# Revit family: PRD_FrankeWS_Mrrs_Mirror_CHRH401-CHRH601
name_source: partatom
category: Furniture
revit_build: Autodesk Revit 2018 (Build: 20190510_1515(x64)
units: mm (PartAtom-declared; Revit-internal decimal feet)

## family parameters
Cut with Voids When Loaded = No
Host = Face
OmniClass Number = 23.40.20.21
OmniClass Title = Toilet and Bath Specialties
Room Calculation Point = No
Shared = No

## types (3) — shared parameters
AssetType = Fixed
Category = Pr_25_71_53_06, Bathroom mirrors
Color = Stainless steel
Default Elevation = 1100 mm
DurationUnit = year
Finish = High polished
Form = Wall mounted
IfcExportAs = IfcFurnitureType
IfcExportType = NOTDEFINED
IntegralAccessories = Stainless steel screws and dowels incl.
MainColor = Stainless steel
Manufacturer = KWC Group AG
ManufacturerName = KWC Group AG
ManufacturerURL = www.kwc.com
Material = Stainless steel
MaterialsGlazing = Stainless steel 1.4301
MirrorMaterial = PRD_AR_StainlessSteel_HighPolished
NBSDescription = Mirrors
NBSReference = 45-35-72/336
NominalDepth = 1 mm  [stored 0.00328084 ft]
ProductInformation = https://pim.kwc.com
Style = Mirror
TypeOfFixing = Screw
URL = www.kwc.com
Uniclass2015Code = Pr_25_71_53_06
Uniclass2015Title = Bathroom mirrors
Uniclass2015Version = Products v1.5
Version = 1
WarrantyDurationUnit = year

## per-type parameters (varying)
| type | BIMObjectName | Description | Features | GrossWeight | Model | ModelNumber | ModelReference | Name | NetWeight | NominalHeight | NominalLength | NominalWidth | Size |
| CHRH401, 400 x 300 mm | PRD_AR_Mirrors_Mirror_CHRH401 | Stainless steel mirror for wall mounting, mirror with a reflective polished surface, material thickness 1 mm, four visible fixation points, incl. stainless steel screws and dowels. size: 400 x 300 mm | stainless steel, 1.00 mm, high polished, wall mounting, 400x300x1 mm (WxHxD) | 1.20 kg | CHRH401 | 2000056953 | CHRH401 | Mirror CHRH401 | 1.00 kg | 300 mm | 400 mm  [stored 1.31234 ft] | 400 mm  [stored 1.31234 ft] | 400 x 300 x 1 mm |
| CHRH501, 500 x 400 mm | PRD_AR_Mirrors_Mirror_CHRH501 | Stainless steel mirror for wall mounting, mirror with a reflective polished surface, material thickness 1 mm, four visible fixation points, incl. stainless steel screws and dowels. size: 500 x 400 mm | stainless steel, 1.00 mm, high polished, wall mounting, 500x400x1 mm (WxHxD) | 1.80 kg | CHRH501 | 2000056955 | CHRH501 | Mirror CHRH501 | 1.60 kg | 400 mm  [stored 1.31234 ft] | 500 mm  [stored 1.64042 ft] | 500 mm  [stored 1.64042 ft] | 500 x 400 x 1 mm |
| CHRH601, 600 x 500 mm | PRD_AR_Mirrors_Mirror_CHRH601 | Stainless steel mirror for wall mounting, mirror with a reflective polished surface, material thickness 1 mm, four visible fixation points, incl. stainless steel screws and dowels. size: 600 x 500 mm | stainless steel, 1.00 mm, high polished, wall mounting, 600x500x1 mm (WxHxD) | 2.60 kg | CHRH601 | 2000056956 | CHRH601 | Mirror CHRH601 | 2.40 kg | 500 mm  [stored 1.64042 ft] | 600 mm | 600 mm | 600 x 500 x 1 mm |

note: [stored X ft] marks values corroborated as IEEE doubles in the binary element streams (Revit-internal decimal feet)

## geometry (parser evidence)
native form markers: Sweep x3
no freeform markers — native parametric forms only
